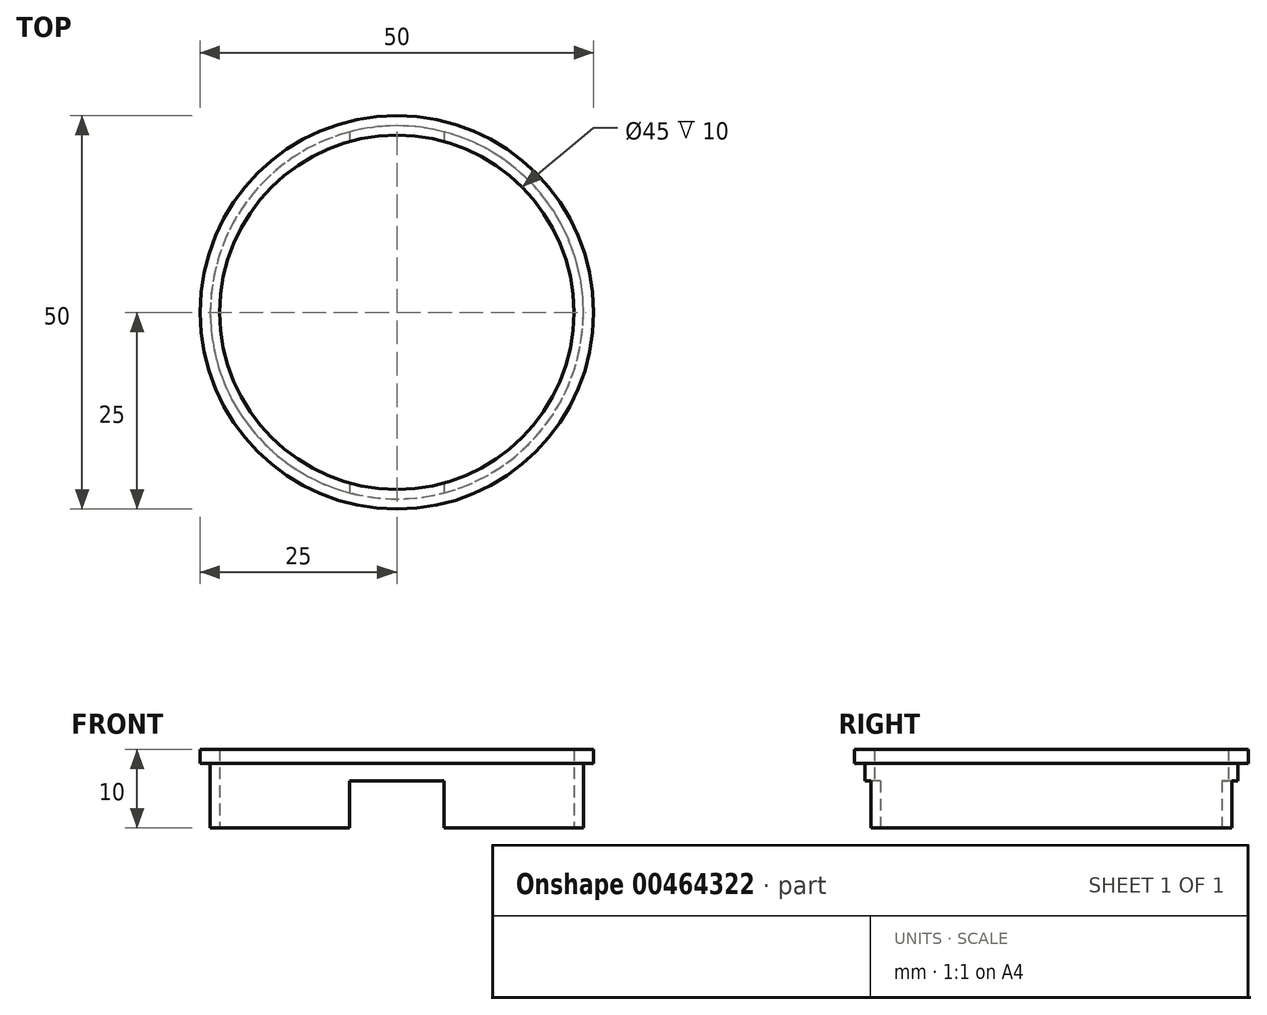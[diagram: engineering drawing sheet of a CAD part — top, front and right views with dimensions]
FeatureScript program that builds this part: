
annotation { "Feature Type Name" : "Feature", "Feature Type Description" : "" }
export const myFeature = defineFeature(function(context is Context, id is Id, definition is map)
    precondition{}
    {
        {
            var Q0;
            Q0=qCreatedBy(makeId("Front.planeOp"),FACE);
            var sketch = newSketch(context, id + "F0", { "sketchPlane" : qUnion([Q0])});
            skLineSegment(sketch, "E0", {"start": v(22.5, 0) * mm, "end": v(22.5, 10) * mm});
            skLineSegment(sketch, "E1", {"start": v(22.5, 10) * mm, "end": v(25, 10) * mm});
            skLineSegment(sketch, "E2", {"start": v(25, 10) * mm, "end": v(25, 8.2) * mm});
            skLineSegment(sketch, "E3", {"start": v(25, 8.2) * mm, "end": v(23.7, 8.2) * mm});
            skLineSegment(sketch, "E4", {"start": v(23.7, 8.2) * mm, "end": v(23.7, 0) * mm});
            skLineSegment(sketch, "E5", {"start": v(23.7, 0) * mm, "end": v(22.5, 0) * mm});
            skLineSegment(sketch, "E6", {"start": v(0, 0) * mm, "end": v(0, 16.08) * mm, "construction": true});
            skSolve(sketch);
        }
        {
            var Q0;
            Q0=makeQuery(id+"F0.imprint","IMPRINT",FACE,{"disambiguationData":[TD([[makeQuery(id+"F0.imprint","IMPRINT",EDGE,{"derivedFrom":sQuery(id+"F0.wireOp",EDGE,"E0")}),-1.0]])]});
            var Q1;
            Q1=sQuery(id+"F0.wireOp",EDGE,"E6");
            revolve(context, id + "F1", {"entities" : qUnion([Q0]), "axis" : qUnion([Q1]), "revolveType" : RevolveType.FULL});
        }
        {
            var Q0;
            Q0=qCreatedBy(makeId("Front.planeOp"),FACE);
            var sketch = newSketch(context, id + "F2", { "sketchPlane" : qUnion([Q0])});
            skLineSegment(sketch, "E7.top", {"start": v(6, 6) * mm, "end": v(-6, 6) * mm});
            skLineSegment(sketch, "E7.left", {"start": v(6, 0) * mm, "end": v(6, 6) * mm});
            skLineSegment(sketch, "E7.right", {"start": v(-6, 0) * mm, "end": v(-6, 6) * mm});
            skPoint(sketch, "E7.middle", {"position": v(0, 0) * mm});
            skLineSegment(sketch, "E8", {"start": v(-6, 0) * mm, "end": v(6, 0) * mm});
            skPoint(sketch, "E7.bottom.end.orphan", {"position": v(-6, -6) * mm});
            skPoint(sketch, "E7.bottom.start.orphan", {"position": v(6, -6) * mm});
            skSolve(sketch);
        }
        {
            var Q0;
            Q0=makeQuery(id+"F2.imprint","IMPRINT",FACE,{"disambiguationData":[TD([[makeQuery(id+"F2.imprint","IMPRINT",EDGE,{"derivedFrom":sQuery(id+"F2.wireOp",EDGE,"E7.top")}),1.0]])]});
            extrude(context, id + "F3", {"entities" : qUnion([Q0]), "operationType" : NewBodyOperationType.REMOVE, "endBound" : BoundingType.THROUGH_ALL, "oppositeDirection" : true, "depth" : 25 * mm, "hasSecondDirection" : true, "secondDirectionBound" : SecondDirectionBoundingType.THROUGH_ALL, "secondDirectionOppositeDirection" : false, "secondDirectionDepth" : 25 * mm});
        }
    });
